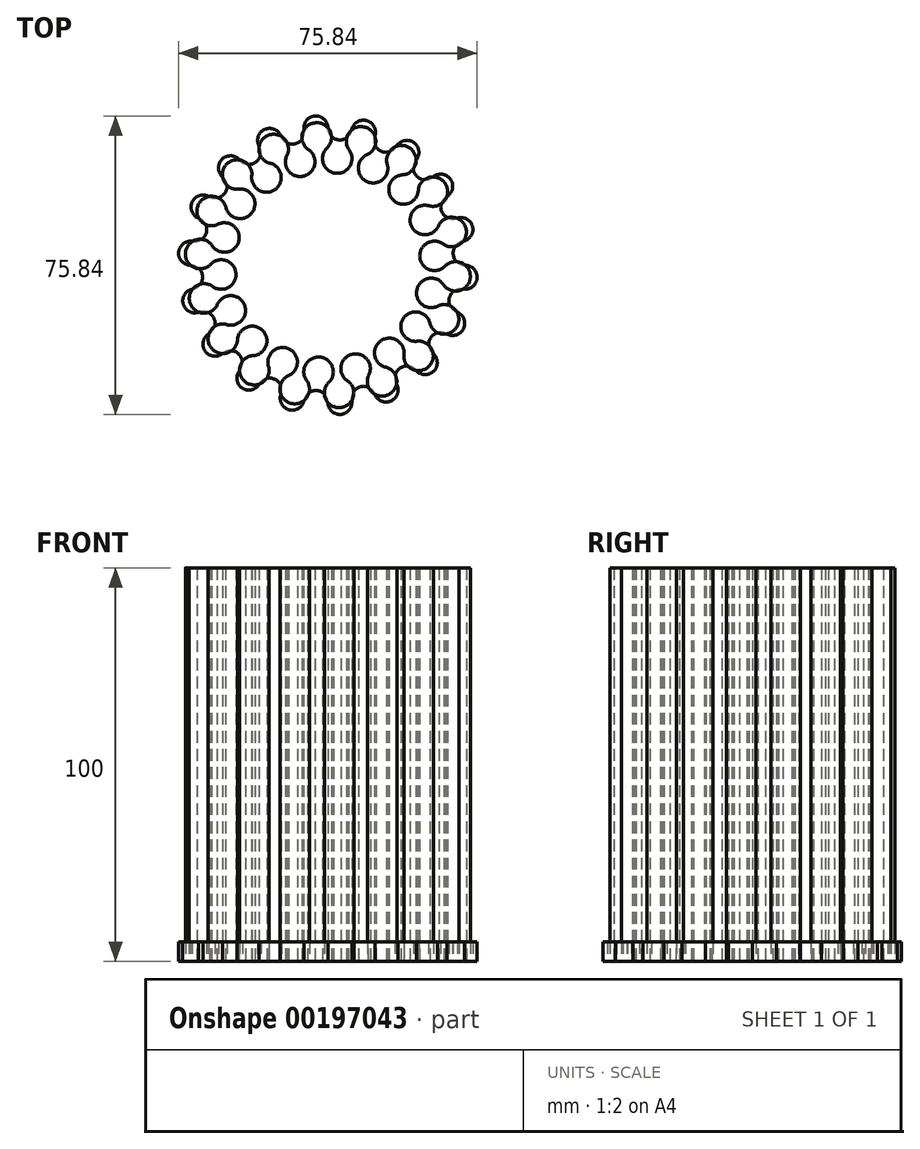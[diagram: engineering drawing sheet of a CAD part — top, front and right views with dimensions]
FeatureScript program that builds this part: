
annotation { "Feature Type Name" : "Feature", "Feature Type Description" : "" }
export const myFeature = defineFeature(function(context is Context, id is Id, definition is map)
    precondition{}
    {
        {
            var Q0;
            Q0=qCreatedBy(makeId("Top.planeOp"),FACE);
            var sketch = newSketch(context, id + "F0", { "sketchPlane" : qUnion([Q0])});
            skCircle(sketch, "E0", {"center": v(0, 0) * mm, "radius": 35 * mm, "construction": true});
            skLineSegment(sketch, "E1", {"start": v(0, 0) * mm, "end": v(-7.64, 43.33) * mm, "construction": true});
            skLineSegment(sketch, "E2", {"start": v(0, 0) * mm, "end": v(7.93, 44.97) * mm, "construction": true});
            skArc(sketch, "E3", {"start": v(0, 35) * mm, "mid": v(-3.32, 37.9) * mm, "end": v(-6.08, 34.47) * mm});
            skArc(sketch, "E4", {"start": v(0, 35) * mm, "mid": v(2.78, 31.83) * mm, "end": v(6.08, 34.47) * mm});
            skArc(sketch, "E5.1.0", {"start": v(-11.97, 32.89) * mm, "mid": v(-16.08, 34.49) * mm, "end": v(-17.5, 30.31) * mm});
            skArc(sketch, "E5.1.1", {"start": v(-11.97, 32.89) * mm, "mid": v(-8.27, 30.86) * mm, "end": v(-6.08, 34.47) * mm});
            skArc(sketch, "E5.2.0", {"start": v(-22.5, 26.81) * mm, "mid": v(-26.9, 26.9) * mm, "end": v(-26.81, 22.5) * mm});
            skArc(sketch, "E5.2.1", {"start": v(-22.5, 26.81) * mm, "mid": v(-18.33, 26.17) * mm, "end": v(-17.5, 30.31) * mm});
            skArc(sketch, "E5.3.0", {"start": v(-30.31, 17.5) * mm, "mid": v(-34.49, 16.08) * mm, "end": v(-32.89, 11.97) * mm});
            skArc(sketch, "E5.3.1", {"start": v(-30.31, 17.5) * mm, "mid": v(-26.17, 18.33) * mm, "end": v(-26.81, 22.5) * mm});
            skArc(sketch, "E5.4.0", {"start": v(-34.47, 6.08) * mm, "mid": v(-37.9, 3.32) * mm, "end": v(-35, 0) * mm});
            skArc(sketch, "E5.4.1", {"start": v(-34.47, 6.08) * mm, "mid": v(-30.86, 8.27) * mm, "end": v(-32.89, 11.97) * mm});
            skArc(sketch, "E5.5.0", {"start": v(-34.47, -6.08) * mm, "mid": v(-36.76, -9.85) * mm, "end": v(-32.89, -11.97) * mm});
            skArc(sketch, "E5.5.1", {"start": v(-34.47, -6.08) * mm, "mid": v(-31.83, -2.78) * mm, "end": v(-35, 0) * mm});
            skArc(sketch, "E5.6.0", {"start": v(-30.31, -17.5) * mm, "mid": v(-31.17, -21.83) * mm, "end": v(-26.81, -22.5) * mm});
            skArc(sketch, "E5.6.1", {"start": v(-30.31, -17.5) * mm, "mid": v(-28.96, -13.5) * mm, "end": v(-32.89, -11.97) * mm});
            skArc(sketch, "E5.7.0", {"start": v(-22.5, -26.81) * mm, "mid": v(-21.83, -31.17) * mm, "end": v(-17.5, -30.31) * mm});
            skArc(sketch, "E5.7.1", {"start": v(-22.5, -26.81) * mm, "mid": v(-22.6, -22.6) * mm, "end": v(-26.81, -22.5) * mm});
            skArc(sketch, "E5.8.0", {"start": v(-11.97, -32.89) * mm, "mid": v(-9.85, -36.76) * mm, "end": v(-6.08, -34.47) * mm});
            skArc(sketch, "E5.8.1", {"start": v(-11.97, -32.89) * mm, "mid": v(-13.5, -28.96) * mm, "end": v(-17.5, -30.31) * mm});
            skArc(sketch, "E5.9.0", {"start": v(0, -35) * mm, "mid": v(3.32, -37.9) * mm, "end": v(6.08, -34.47) * mm});
            skArc(sketch, "E5.9.1", {"start": v(0, -35) * mm, "mid": v(-2.78, -31.83) * mm, "end": v(-6.08, -34.47) * mm});
            skArc(sketch, "E5.10.0", {"start": v(11.97, -32.89) * mm, "mid": v(16.08, -34.49) * mm, "end": v(17.5, -30.31) * mm});
            skArc(sketch, "E5.10.1", {"start": v(11.97, -32.89) * mm, "mid": v(8.27, -30.86) * mm, "end": v(6.08, -34.47) * mm});
            skArc(sketch, "E5.11.0", {"start": v(22.5, -26.81) * mm, "mid": v(26.9, -26.9) * mm, "end": v(26.81, -22.5) * mm});
            skArc(sketch, "E5.11.1", {"start": v(22.5, -26.81) * mm, "mid": v(18.33, -26.17) * mm, "end": v(17.5, -30.31) * mm});
            skArc(sketch, "E5.12.0", {"start": v(30.31, -17.5) * mm, "mid": v(34.49, -16.08) * mm, "end": v(32.89, -11.97) * mm});
            skArc(sketch, "E5.12.1", {"start": v(30.31, -17.5) * mm, "mid": v(26.17, -18.33) * mm, "end": v(26.81, -22.5) * mm});
            skArc(sketch, "E5.13.0", {"start": v(34.47, -6.08) * mm, "mid": v(37.9, -3.32) * mm, "end": v(35, 0) * mm});
            skArc(sketch, "E5.13.1", {"start": v(34.47, -6.08) * mm, "mid": v(30.86, -8.27) * mm, "end": v(32.89, -11.97) * mm});
            skArc(sketch, "E5.14.0", {"start": v(34.47, 6.08) * mm, "mid": v(36.76, 9.85) * mm, "end": v(32.89, 11.97) * mm});
            skArc(sketch, "E5.14.1", {"start": v(34.47, 6.08) * mm, "mid": v(31.83, 2.78) * mm, "end": v(35, 0) * mm});
            skArc(sketch, "E5.15.0", {"start": v(30.31, 17.5) * mm, "mid": v(31.17, 21.83) * mm, "end": v(26.81, 22.5) * mm});
            skArc(sketch, "E5.15.1", {"start": v(30.31, 17.5) * mm, "mid": v(28.96, 13.5) * mm, "end": v(32.89, 11.97) * mm});
            skArc(sketch, "E5.16.0", {"start": v(22.5, 26.81) * mm, "mid": v(21.83, 31.17) * mm, "end": v(17.5, 30.31) * mm});
            skArc(sketch, "E5.16.1", {"start": v(22.5, 26.81) * mm, "mid": v(22.6, 22.6) * mm, "end": v(26.81, 22.5) * mm});
            skArc(sketch, "E5.17.0", {"start": v(11.97, 32.89) * mm, "mid": v(9.85, 36.76) * mm, "end": v(6.08, 34.47) * mm});
            skArc(sketch, "E5.17.1", {"start": v(11.97, 32.89) * mm, "mid": v(13.5, 28.96) * mm, "end": v(17.5, 30.31) * mm});
            skSolve(sketch);
        }
        {
            var Q0;
            Q0 = qSketchRegion(id + "F0", true);
            extrude(context, id + "F1", {"entities" : qUnion([Q0]), "depth" : 5 * mm});
        }
        {
            var Q0;
            Q0=qCreatedBy(makeId("Top.planeOp"),FACE);
            var sketch = newSketch(context, id + "F2", { "sketchPlane" : qUnion([Q0])});
            skCircle(sketch, "E6", {"center": v(0, 0) * mm, "radius": 30 * mm, "construction": true});
            skLineSegment(sketch, "E7", {"start": v(0, 0) * mm, "end": v(-8.36, 47.4) * mm, "construction": true});
            skLineSegment(sketch, "E8", {"start": v(0, 0) * mm, "end": v(7.73, 43.82) * mm, "construction": true});
            skArc(sketch, "E9", {"start": v(0, 30) * mm, "mid": v(-3.17, 36.19) * mm, "end": v(-5.2, 29.54) * mm});
            skArc(sketch, "E10", {"start": v(0, 30) * mm, "mid": v(2.04, 23.36) * mm, "end": v(5.2, 29.54) * mm});
            skArc(sketch, "E11.1.0", {"start": v(-10.26, 28.2) * mm, "mid": v(-15.35, 32.92) * mm, "end": v(-15, 25.98) * mm});
            skArc(sketch, "E11.1.1", {"start": v(-10.26, 28.2) * mm, "mid": v(-6.07, 22.65) * mm, "end": v(-5.2, 29.54) * mm});
            skArc(sketch, "E11.2.0", {"start": v(-19.28, 22.98) * mm, "mid": v(-25.68, 25.68) * mm, "end": v(-22.98, 19.28) * mm});
            skArc(sketch, "E11.2.1", {"start": v(-19.28, 22.98) * mm, "mid": v(-13.45, 19.2) * mm, "end": v(-15, 25.98) * mm});
            skArc(sketch, "E11.3.0", {"start": v(-25.98, 15) * mm, "mid": v(-32.92, 15.35) * mm, "end": v(-28.2, 10.26) * mm});
            skArc(sketch, "E11.3.1", {"start": v(-25.98, 15) * mm, "mid": v(-19.2, 13.45) * mm, "end": v(-22.98, 19.28) * mm});
            skArc(sketch, "E11.4.0", {"start": v(-29.54, 5.2) * mm, "mid": v(-36.19, 3.17) * mm, "end": v(-30, 0) * mm});
            skArc(sketch, "E11.4.1", {"start": v(-29.54, 5.2) * mm, "mid": v(-22.65, 6.07) * mm, "end": v(-28.2, 10.26) * mm});
            skArc(sketch, "E11.5.0", {"start": v(-29.54, -5.2) * mm, "mid": v(-35.09, -9.4) * mm, "end": v(-28.2, -10.26) * mm});
            skArc(sketch, "E11.5.1", {"start": v(-29.54, -5.2) * mm, "mid": v(-23.36, -2.04) * mm, "end": v(-30, 0) * mm});
            skArc(sketch, "E11.6.0", {"start": v(-25.98, -15) * mm, "mid": v(-29.75, -20.83) * mm, "end": v(-22.98, -19.28) * mm});
            skArc(sketch, "E11.6.1", {"start": v(-25.98, -15) * mm, "mid": v(-21.25, -9.9) * mm, "end": v(-28.2, -10.26) * mm});
            skArc(sketch, "E11.7.0", {"start": v(-19.28, -22.98) * mm, "mid": v(-20.83, -29.75) * mm, "end": v(-15, -25.98) * mm});
            skArc(sketch, "E11.7.1", {"start": v(-19.28, -22.98) * mm, "mid": v(-16.58, -16.58) * mm, "end": v(-22.98, -19.28) * mm});
            skArc(sketch, "E11.8.0", {"start": v(-10.26, -28.2) * mm, "mid": v(-9.4, -35.09) * mm, "end": v(-5.2, -29.54) * mm});
            skArc(sketch, "E11.8.1", {"start": v(-10.26, -28.2) * mm, "mid": v(-9.9, -21.25) * mm, "end": v(-15, -25.98) * mm});
            skArc(sketch, "E11.9.0", {"start": v(0, -30) * mm, "mid": v(3.17, -36.19) * mm, "end": v(5.2, -29.54) * mm});
            skArc(sketch, "E11.9.1", {"start": v(0, -30) * mm, "mid": v(-2.04, -23.36) * mm, "end": v(-5.2, -29.54) * mm});
            skArc(sketch, "E11.10.0", {"start": v(10.26, -28.2) * mm, "mid": v(15.35, -32.92) * mm, "end": v(15, -25.98) * mm});
            skArc(sketch, "E11.10.1", {"start": v(10.26, -28.2) * mm, "mid": v(6.07, -22.65) * mm, "end": v(5.2, -29.54) * mm});
            skArc(sketch, "E11.11.0", {"start": v(19.28, -22.98) * mm, "mid": v(25.68, -25.68) * mm, "end": v(22.98, -19.28) * mm});
            skArc(sketch, "E11.11.1", {"start": v(19.28, -22.98) * mm, "mid": v(13.45, -19.2) * mm, "end": v(15, -25.98) * mm});
            skArc(sketch, "E11.12.0", {"start": v(25.98, -15) * mm, "mid": v(32.92, -15.35) * mm, "end": v(28.2, -10.26) * mm});
            skArc(sketch, "E11.12.1", {"start": v(25.98, -15) * mm, "mid": v(19.2, -13.45) * mm, "end": v(22.98, -19.28) * mm});
            skArc(sketch, "E11.13.0", {"start": v(29.54, -5.2) * mm, "mid": v(36.19, -3.17) * mm, "end": v(30, 0) * mm});
            skArc(sketch, "E11.13.1", {"start": v(29.54, -5.2) * mm, "mid": v(22.65, -6.07) * mm, "end": v(28.2, -10.26) * mm});
            skArc(sketch, "E11.14.0", {"start": v(29.54, 5.2) * mm, "mid": v(35.09, 9.4) * mm, "end": v(28.2, 10.26) * mm});
            skArc(sketch, "E11.14.1", {"start": v(29.54, 5.2) * mm, "mid": v(23.36, 2.04) * mm, "end": v(30, 0) * mm});
            skArc(sketch, "E11.15.0", {"start": v(25.98, 15) * mm, "mid": v(29.75, 20.83) * mm, "end": v(22.98, 19.28) * mm});
            skArc(sketch, "E11.15.1", {"start": v(25.98, 15) * mm, "mid": v(21.25, 9.9) * mm, "end": v(28.2, 10.26) * mm});
            skArc(sketch, "E11.16.0", {"start": v(19.28, 22.98) * mm, "mid": v(20.83, 29.75) * mm, "end": v(15, 25.98) * mm});
            skArc(sketch, "E11.16.1", {"start": v(19.28, 22.98) * mm, "mid": v(16.58, 16.58) * mm, "end": v(22.98, 19.28) * mm});
            skArc(sketch, "E11.17.0", {"start": v(10.26, 28.2) * mm, "mid": v(9.4, 35.09) * mm, "end": v(5.2, 29.54) * mm});
            skArc(sketch, "E11.17.1", {"start": v(10.26, 28.2) * mm, "mid": v(9.9, 21.25) * mm, "end": v(15, 25.98) * mm});
            skSolve(sketch);
        }
        {
            var Q0;
            Q0=makeQuery(id+"F2.imprint","IMPRINT",FACE,{"disambiguationData":[TD([[makeQuery(id+"F2.imprint","IMPRINT",EDGE,{"derivedFrom":sQuery(id+"F2.wireOp",EDGE,"E9")}),1.0]])]});
            extrude(context, id + "F3", {"entities" : qUnion([Q0]), "depth" : 100 * mm});
        }
    });
